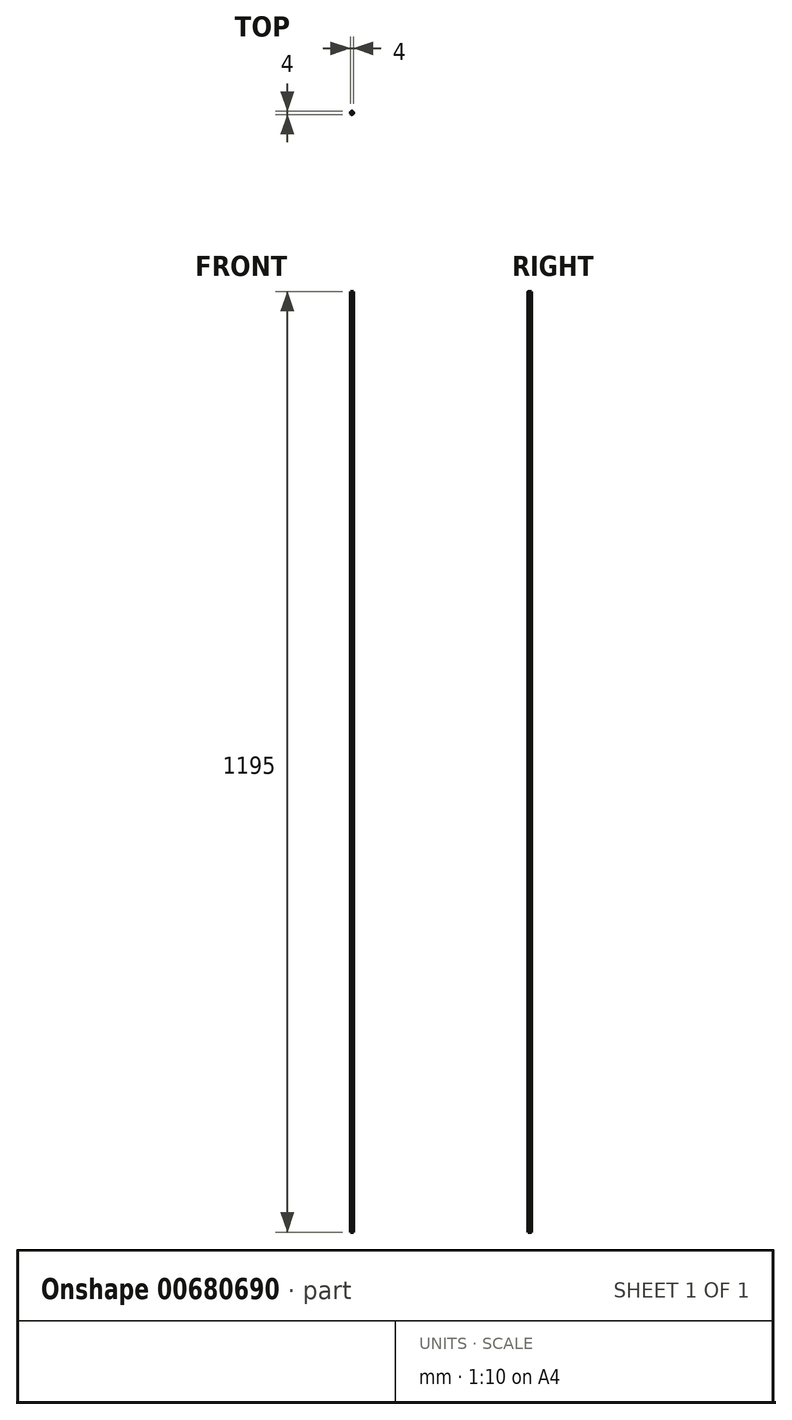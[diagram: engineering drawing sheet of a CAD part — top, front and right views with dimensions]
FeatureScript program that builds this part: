
annotation { "Feature Type Name" : "Feature", "Feature Type Description" : "" }
export const myFeature = defineFeature(function(context is Context, id is Id, definition is map)
    precondition{}
    {
        {
            var Q0;
            Q0=qCreatedBy(makeId("Top.planeOp"),FACE);
            var sketch = newSketch(context, id + "F0", { "sketchPlane" : qUnion([Q0])});
            skCircle(sketch, "E0", {"center": v(0, 0) * mm, "radius": 2 * mm});
            skSolve(sketch);
        }
        {
            var Q0;
            Q0=makeQuery(id+"F0.imprint","IMPRINT",FACE,{"disambiguationData":[TD([[makeQuery(id+"F0.imprint","IMPRINT",EDGE,{"derivedFrom":sQuery(id+"F0.wireOp",EDGE,"E0")}),1.0]])]});
            extrude(context, id + "F1", {"entities" : qUnion([Q0]), "depth" : (1120 + 75) * mm, "offsetDistance" : 25 * mm});
        }
    });
